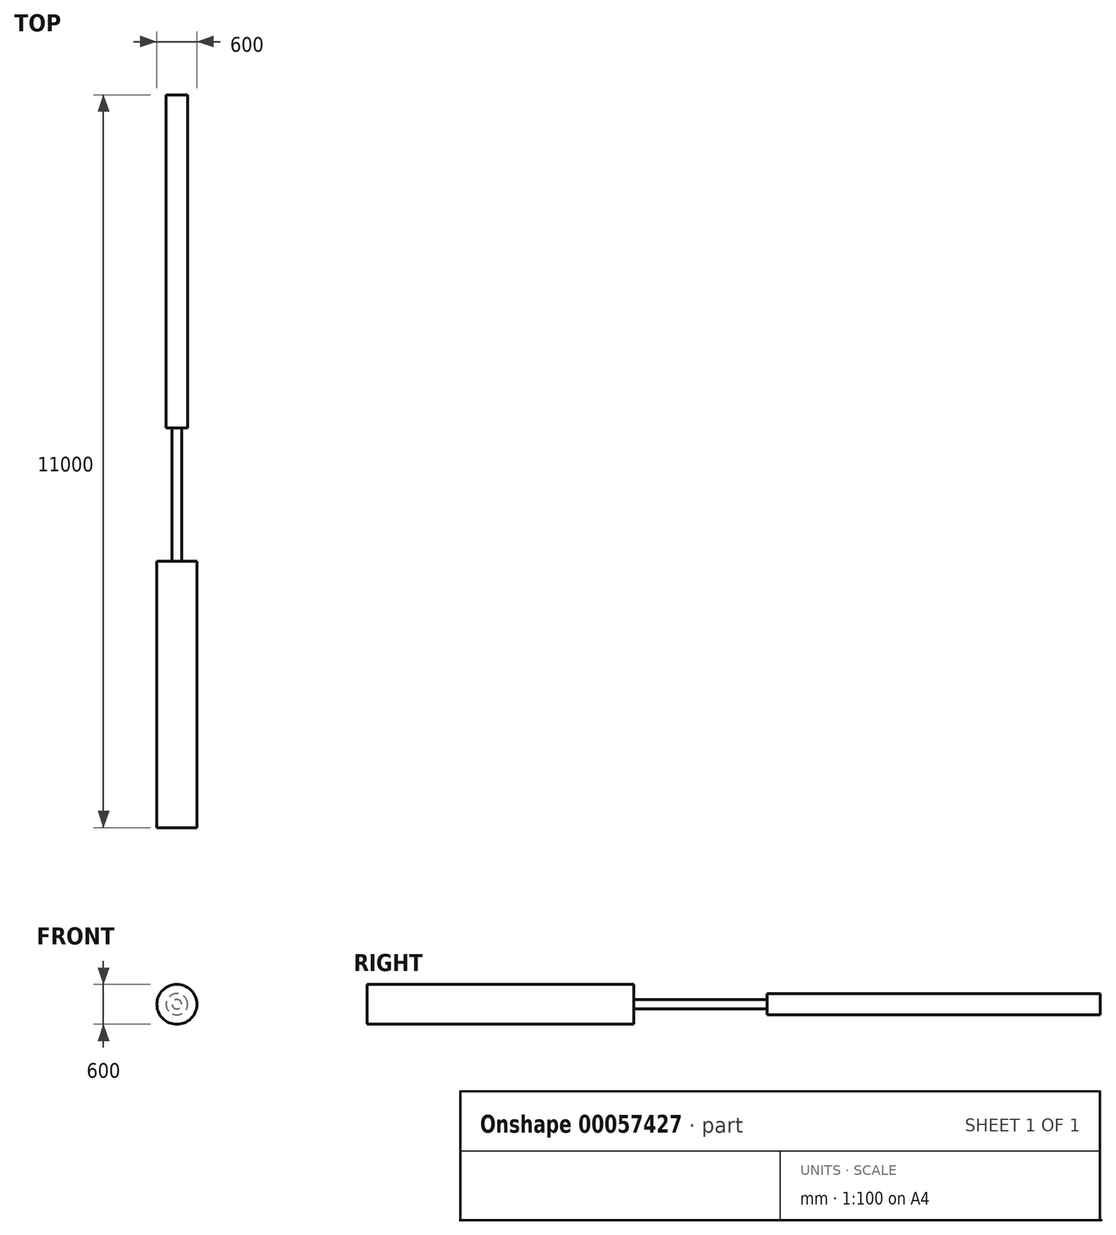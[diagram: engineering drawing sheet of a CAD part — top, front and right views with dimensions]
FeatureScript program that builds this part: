
annotation { "Feature Type Name" : "Feature", "Feature Type Description" : "" }
export const myFeature = defineFeature(function(context is Context, id is Id, definition is map)
    precondition{}
    {
        {
            var Q0;
            Q0=qCreatedBy(makeId("Right.planeOp"),FACE);
            var sketch = newSketch(context, id + "F0", { "sketchPlane" : qUnion([Q0])});
            skLineSegment(sketch, "E0", {"start": v(0, 0) * mm, "end": v(0, 300) * mm});
            skLineSegment(sketch, "E1", {"start": v(0, 300) * mm, "end": v(4000, 300) * mm});
            skLineSegment(sketch, "E2", {"start": v(4000, 300) * mm, "end": v(4000, 71.16) * mm});
            skLineSegment(sketch, "E3", {"start": v(4000, 71.16) * mm, "end": v(6000, 71.16) * mm});
            skLineSegment(sketch, "E4", {"start": v(6000, 71.16) * mm, "end": v(6000, 160.47) * mm});
            skLineSegment(sketch, "E5", {"start": v(6000, 160.47) * mm, "end": v(11000, 160.47) * mm});
            skLineSegment(sketch, "E6", {"start": v(11000, 160.47) * mm, "end": v(11000, 0) * mm});
            skLineSegment(sketch, "E7", {"start": v(11000, 0) * mm, "end": v(0, 0) * mm});
            skSolve(sketch);
        }
        {
            var Q0;
            Q0=makeQuery(id+"F0.imprint","IMPRINT",FACE,{"disambiguationData":[TD([[makeQuery(id+"F0.imprint","IMPRINT",EDGE,{"derivedFrom":sQuery(id+"F0.wireOp",EDGE,"E0")}),-1.0]])]});
            var Q1;
            Q1=sQuery(id+"F0.wireOp",EDGE,"E7");
            revolve(context, id + "F1", {"entities" : qUnion([Q0]), "axis" : qUnion([Q1]), "revolveType" : RevolveType.FULL});
        }
    });
